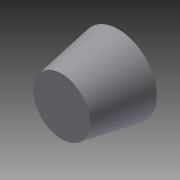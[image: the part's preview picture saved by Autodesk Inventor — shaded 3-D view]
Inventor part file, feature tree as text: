
AUTODESK INVENTOR PART (.ipt)
format: ipt  version: 2015 (Build 190159000, 159)  size: 120,832 bytes
history: native  units: mm
features: extrude x2, sketch x2
ambient origin geometry x8: Origin, YZ Plane, XZ Plane, XY Plane, X Axis, Y Axis, Z Axis, Center Point
bodies: Solid1 (feature_tree)
feature tree (4):
  extrude  "Extrusion1"  Depth=350.0mm
  extrude  "Extrusion2"  Depth=315.0mm
  sketch  "Sketch1"  dims[d0=350.0mm d1=350.0mm d2=1.745329mm]
  sketch  "Sketch3"  dims[d3=35.0mm d4=315.0mm d5=-1.745329mm]
